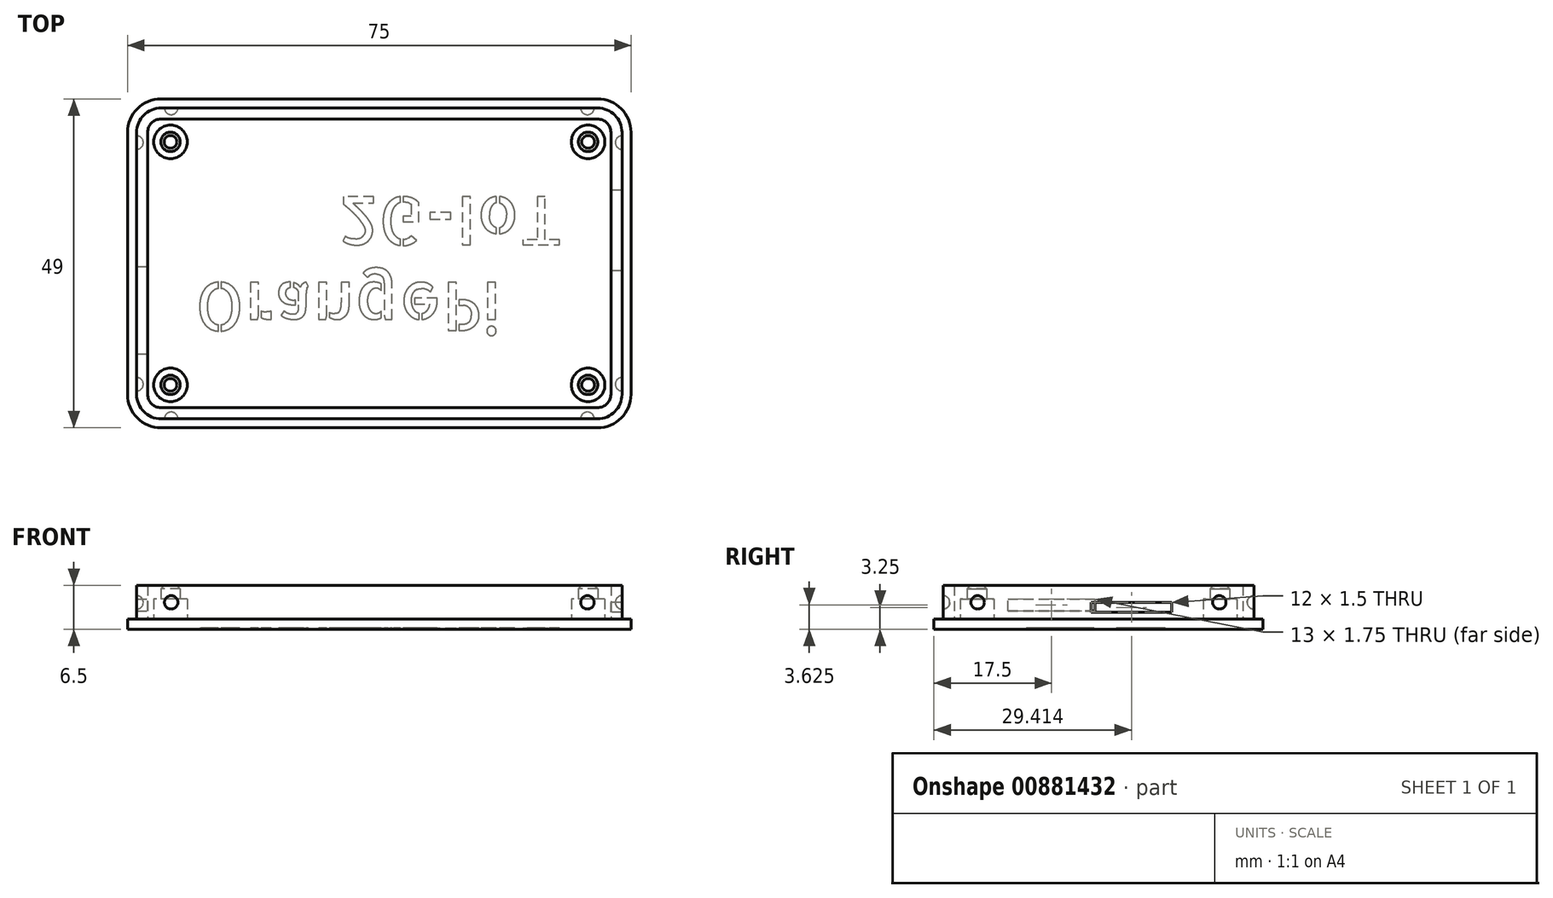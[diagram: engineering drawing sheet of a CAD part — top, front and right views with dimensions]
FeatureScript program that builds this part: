
annotation { "Feature Type Name" : "Feature", "Feature Type Description" : "" }
export const myFeature = defineFeature(function(context is Context, id is Id, definition is map)
    precondition{}
    {
        {
            assignVariable(context, id + "F0", {"name" : "PCBThickness", "anyValue" : 2});
        }
        {
            assignVariable(context, id + "F1", {"name" : "PCBClarence", "anyValue" : 3});
        }
        {
            assignVariable(context, id + "F2", {"name" : "WallThickness", "anyValue" : 3});
        }
        {
            assignVariable(context, id + "F3", {"name" : "OuterFilletRadius", "anyValue" : 5});
        }
        {
            var Q0;
            Q0=qCreatedBy(makeId("Top.planeOp"),FACE);
            var sketch = newSketch(context, id + "F4", { "sketchPlane" : qUnion([Q0])});
            skLineSegment(sketch, "E0.bottom", {"start": v(37.5, 24.5) * mm, "end": v(-37.5, 24.5) * mm});
            skLineSegment(sketch, "E0.top", {"start": v(37.5, -24.5) * mm, "end": v(-37.5, -24.5) * mm});
            skLineSegment(sketch, "E0.left", {"start": v(37.5, 24.5) * mm, "end": v(37.5, -24.5) * mm});
            skLineSegment(sketch, "E0.right", {"start": v(-37.5, 24.5) * mm, "end": v(-37.5, -24.5) * mm});
            skPoint(sketch, "E0.middle", {"position": v(0, 0) * mm});
            skSolve(sketch);
        }
        {
            var Q0;
            Q0 = qSketchRegion(id + "F4", true);
            extrude(context, id + "F5", {"entities" : qUnion([Q0]), "depth" : (getVariable(context, 'WallThickness') + getVariable(context, 'PCBThickness') + getVariable(context, 'PCBClarence')) * mm, "offsetDistance" : 25 * mm});
        }
        {
            var Q0;
            Q0=makeQuery(id+"F5.opExtrude","SWEPT_EDGE",EDGE,{"disambiguationData":[OSD([sQuery(id+"F4.wireOp",EDGE,"E0.top"),sQuery(id+"F4.wireOp",EDGE,"E0.right")])]});
            var Q1;
            Q1=makeQuery(id+"F5.opExtrude","SWEPT_EDGE",EDGE,{"disambiguationData":[OSD([sQuery(id+"F4.wireOp",EDGE,"E0.top"),sQuery(id+"F4.wireOp",EDGE,"E0.left")])]});
            var Q2;
            Q2=makeQuery(id+"F5.opExtrude","SWEPT_EDGE",EDGE,{"disambiguationData":[OSD([sQuery(id+"F4.wireOp",EDGE,"E0.bottom"),sQuery(id+"F4.wireOp",EDGE,"E0.left")])]});
            var Q3;
            Q3=makeQuery(id+"F5.opExtrude","SWEPT_EDGE",EDGE,{"disambiguationData":[OSD([sQuery(id+"F4.wireOp",EDGE,"E0.bottom"),sQuery(id+"F4.wireOp",EDGE,"E0.right")])]});
            fillet(context, id + "F6", {"entities" : qUnion([Q0, Q1, Q2, Q3]), "radius" : (getVariable(context, 'OuterFilletRadius')) * mm, "tangentPropagation" : true, "allowEdgeOverflow" : false});
        }
        {
            var Q0;
            Q0=makeQuery(id+"F5.opExtrude","CAP_FACE",FACE,{"disambiguationData":[OSD([sQuery(id+"F4.wireOp",EDGE,"E0.bottom"),sQuery(id+"F4.wireOp",EDGE,"E0.top"),sQuery(id+"F4.wireOp",EDGE,"E0.left"),sQuery(id+"F4.wireOp",EDGE,"E0.right")])],"isStart":false});
            shell(context, id + "F7", {"entities" : qUnion([Q0]), "thickness" : (getVariable(context, 'WallThickness')) * mm});
        }
        {
            var Q0;
            Q0=makeQuery(id+"F7.opShell","OFFSET_FACE",FACE,{"disambiguationData":[OSD([sQuery(id+"F4.wireOp",EDGE,"E0.bottom"),sQuery(id+"F4.wireOp",EDGE,"E0.top"),sQuery(id+"F4.wireOp",EDGE,"E0.left"),sQuery(id+"F4.wireOp",EDGE,"E0.right")])]});
            var sketch = newSketch(context, id + "F8", { "sketchPlane" : qUnion([Q0])});
            skLineSegment(sketch, "E1.bottom", {"start": v(31.1, 18.1) * mm, "end": v(-31.1, 18.1) * mm, "construction": true});
            skLineSegment(sketch, "E1.top", {"start": v(31.1, -18.1) * mm, "end": v(-31.1, -18.1) * mm, "construction": true});
            skLineSegment(sketch, "E1.left", {"start": v(31.1, 18.1) * mm, "end": v(31.1, -18.1) * mm, "construction": true});
            skLineSegment(sketch, "E1.right", {"start": v(-31.1, 18.1) * mm, "end": v(-31.1, -18.1) * mm, "construction": true});
            skPoint(sketch, "E1.middle", {"position": v(0, 0) * mm});
            skCircle(sketch, "E2", {"center": v(-31.1, 18.1) * mm, "radius": 2.5 * mm});
            skCircle(sketch, "E3", {"center": v(-31.1, -18.1) * mm, "radius": 2.5 * mm});
            skCircle(sketch, "E4", {"center": v(31.1, 18.1) * mm, "radius": 2.5 * mm});
            skCircle(sketch, "E5", {"center": v(31.1, -18.1) * mm, "radius": 2.5 * mm});
            skSolve(sketch);
        }
        {
            var Q0;
            Q0 = qSketchRegion(id + "F8", true);
            extrude(context, id + "F9", {"entities" : qUnion([Q0]), "operationType" : NewBodyOperationType.ADD, "depth" : 3 * mm, "offsetDistance" : 25 * mm});
        }
        {
            var Q0;
            Q0=makeQuery(id+"F9.opExtrude","CAP_FACE",FACE,{"disambiguationData":[OSD([sQuery(id+"F8.wireOp",EDGE,"E2")])],"isStart":false});
            var sketch = newSketch(context, id + "F10", { "sketchPlane" : qUnion([Q0])});
            skLineSegment(sketch, "E6.bottom", {"start": v(-31.1, 18.1) * mm, "end": v(31.1, 18.1) * mm, "construction": true});
            skLineSegment(sketch, "E6.top", {"start": v(-31.1, -18.1) * mm, "end": v(31.1, -18.1) * mm, "construction": true});
            skLineSegment(sketch, "E6.left", {"start": v(-31.1, 18.1) * mm, "end": v(-31.1, -18.1) * mm, "construction": true});
            skLineSegment(sketch, "E6.right", {"start": v(31.1, 18.1) * mm, "end": v(31.1, -18.1) * mm, "construction": true});
            skCircle(sketch, "E7", {"center": v(-31.1, 18.1) * mm, "radius": 1.45 * mm});
            skCircle(sketch, "E8", {"center": v(31.1, 18.1) * mm, "radius": 1.45 * mm});
            skCircle(sketch, "E9", {"center": v(-31.1, -18.1) * mm, "radius": 1.45 * mm});
            skCircle(sketch, "E10", {"center": v(31.1, -18.1) * mm, "radius": 1.45 * mm});
            skSolve(sketch);
        }
        {
            var Q0;
            Q0 = qSketchRegion(id + "F10", true);
            extrude(context, id + "F11", {"entities" : qUnion([Q0]), "operationType" : NewBodyOperationType.ADD, "depth" : 2 * mm, "offsetDistance" : 25 * mm});
        }
        {
            var Q0;
            Q0=makeQuery(id+"F5.opExtrude","CAP_FACE",FACE,{"disambiguationData":[OSD([sQuery(id+"F4.wireOp",EDGE,"E0.bottom"),sQuery(id+"F4.wireOp",EDGE,"E0.top"),sQuery(id+"F4.wireOp",EDGE,"E0.left"),sQuery(id+"F4.wireOp",EDGE,"E0.right")])],"isStart":false});
            var sketch = newSketch(context, id + "F12", { "sketchPlane" : qUnion([Q0])});
            skLineSegment(sketch, "E11", {"start": v(-32.5, 24.5) * mm, "end": v(32.5, 24.5) * mm});
            skLineSegment(sketch, "E12", {"start": v(37.5, 19.5) * mm, "end": v(37.5, -19.5) * mm});
            skLineSegment(sketch, "E13", {"start": v(32.5, -24.5) * mm, "end": v(-32.5, -24.5) * mm});
            skLineSegment(sketch, "E14", {"start": v(-37.5, -19.5) * mm, "end": v(-37.5, 19.5) * mm});
            skArc(sketch, "E15", {"start": v(-32.5, 24.5) * mm, "mid": v(-36.04, 23.04) * mm, "end": v(-37.5, 19.5) * mm});
            skArc(sketch, "E16", {"start": v(37.5, 19.5) * mm, "mid": v(36.04, 23.04) * mm, "end": v(32.5, 24.5) * mm});
            skArc(sketch, "E17", {"start": v(32.5, -24.5) * mm, "mid": v(36.04, -23.04) * mm, "end": v(37.5, -19.5) * mm});
            skArc(sketch, "E18", {"start": v(-37.5, -19.5) * mm, "mid": v(-36.04, -23.04) * mm, "end": v(-32.5, -24.5) * mm});
            skLineSegment(sketch, "E19", {"start": v(-32.5, 24.5) * mm, "end": v(-32.5, 23.15) * mm, "construction": true});
            skLineSegment(sketch, "E20", {"start": v(-32.5, 23.15) * mm, "end": v(32.5, 23.15) * mm});
            skLineSegment(sketch, "E21", {"start": v(32.5, 23.15) * mm, "end": v(32.5, 24.5) * mm, "construction": true});
            skLineSegment(sketch, "E22", {"start": v(37.5, 19.5) * mm, "end": v(36.15, 19.5) * mm, "construction": true});
            skLineSegment(sketch, "E23", {"start": v(36.15, 19.5) * mm, "end": v(36.15, -19.5) * mm});
            skLineSegment(sketch, "E24", {"start": v(36.15, -19.5) * mm, "end": v(37.5, -19.5) * mm, "construction": true});
            skLineSegment(sketch, "E25", {"start": v(32.5, -24.5) * mm, "end": v(32.5, -23.15) * mm, "construction": true});
            skLineSegment(sketch, "E26", {"start": v(32.5, -23.15) * mm, "end": v(-32.5, -23.15) * mm});
            skLineSegment(sketch, "E27", {"start": v(-32.5, -23.15) * mm, "end": v(-32.5, -24.5) * mm, "construction": true});
            skLineSegment(sketch, "E28", {"start": v(-37.5, -19.5) * mm, "end": v(-36.15, -19.5) * mm, "construction": true});
            skLineSegment(sketch, "E29", {"start": v(-36.15, -19.5) * mm, "end": v(-36.15, 19.5) * mm});
            skLineSegment(sketch, "E30", {"start": v(-36.15, 19.5) * mm, "end": v(-37.5, 19.5) * mm, "construction": true});
            skArc(sketch, "E31", {"start": v(-32.5, 23.15) * mm, "mid": v(-35.08, 22.08) * mm, "end": v(-36.15, 19.5) * mm});
            skArc(sketch, "E32", {"start": v(36.15, 19.5) * mm, "mid": v(35.08, 22.08) * mm, "end": v(32.5, 23.15) * mm});
            skArc(sketch, "E33", {"start": v(32.5, -23.15) * mm, "mid": v(35.08, -22.08) * mm, "end": v(36.15, -19.5) * mm});
            skArc(sketch, "E34", {"start": v(-36.15, -19.5) * mm, "mid": v(-35.08, -22.08) * mm, "end": v(-32.5, -23.15) * mm});
            skSolve(sketch);
        }
        {
            var Q0;
            Q0 = qSketchRegion(id + "F12", true);
            extrude(context, id + "F13", {"entities" : qUnion([Q0]), "operationType" : NewBodyOperationType.REMOVE, "oppositeDirection" : true, "depth" : 5 * mm, "offsetDistance" : 25 * mm});
        }
        {
            var Q0;
            Q0=makeQuery(id+"F13.boolean.opBoolean","COPY",FACE,{"derivedFrom":makeQuery(id+"F13.opExtrude","SWEPT_FACE",FACE,{"disambiguationData":[OSD([sQuery(id+"F12.wireOp",EDGE,"E26")])]})});
            var sketch = newSketch(context, id + "F14", { "sketchPlane" : qUnion([Q0])});
            skLineSegment(sketch, "E35", {"start": v(-32.5, 5.5) * mm, "end": v(32.5, 5.5) * mm, "construction": true});
            skCircle(sketch, "E36", {"center": v(-31, 5.5) * mm, "radius": 1 * mm});
            skCircle(sketch, "E37", {"center": v(31, 5.5) * mm, "radius": 1 * mm});
            skSolve(sketch);
        }
        {
            var Q0;
            Q0 = qSketchRegion(id + "F14", true);
            extrude(context, id + "F15", {"entities" : qUnion([Q0]), "operationType" : NewBodyOperationType.REMOVE, "oppositeDirection" : true, "depth" : 1 * mm, "offsetDistance" : 25 * mm});
        }
        {
            var Q0;
            Q0=makeQuery(id+"F13.boolean.opBoolean","COPY",FACE,{"derivedFrom":makeQuery(id+"F13.opExtrude","SWEPT_FACE",FACE,{"disambiguationData":[OSD([sQuery(id+"F12.wireOp",EDGE,"E23")])]})});
            var sketch = newSketch(context, id + "F16", { "sketchPlane" : qUnion([Q0])});
            skLineSegment(sketch, "E38", {"start": v(-19.5, 5.5) * mm, "end": v(19.5, 5.5) * mm, "construction": true});
            skCircle(sketch, "E39", {"center": v(-18, 5.5) * mm, "radius": 1 * mm});
            skCircle(sketch, "E40", {"center": v(18, 5.5) * mm, "radius": 1 * mm});
            skSolve(sketch);
        }
        {
            var Q0;
            Q0 = qSketchRegion(id + "F16", true);
            extrude(context, id + "F17", {"entities" : qUnion([Q0]), "operationType" : NewBodyOperationType.REMOVE, "oppositeDirection" : true, "depth" : 1 * mm, "offsetDistance" : 25 * mm});
        }
        {
            var Q0;
            Q0=makeQuery(id+"F13.boolean.opBoolean","COPY",FACE,{"derivedFrom":makeQuery(id+"F13.opExtrude","SWEPT_FACE",FACE,{"disambiguationData":[OSD([sQuery(id+"F12.wireOp",EDGE,"E20")])]})});
            var sketch = newSketch(context, id + "F18", { "sketchPlane" : qUnion([Q0])});
            skLineSegment(sketch, "E41", {"start": v(-32.5, 5.5) * mm, "end": v(32.5, 5.5) * mm, "construction": true});
            skCircle(sketch, "E42", {"center": v(-31, 5.5) * mm, "radius": 1 * mm});
            skCircle(sketch, "E43", {"center": v(31, 5.5) * mm, "radius": 1 * mm});
            skSolve(sketch);
        }
        {
            var Q0;
            Q0 = qSketchRegion(id + "F18", true);
            extrude(context, id + "F19", {"entities" : qUnion([Q0]), "operationType" : NewBodyOperationType.REMOVE, "oppositeDirection" : true, "depth" : 1 * mm, "offsetDistance" : 25 * mm});
        }
        {
            var Q0;
            Q0=makeQuery(id+"F13.boolean.opBoolean","COPY",FACE,{"derivedFrom":makeQuery(id+"F13.opExtrude","SWEPT_FACE",FACE,{"disambiguationData":[OSD([sQuery(id+"F12.wireOp",EDGE,"E29")])]})});
            var sketch = newSketch(context, id + "F20", { "sketchPlane" : qUnion([Q0])});
            skLineSegment(sketch, "E44", {"start": v(-19.5, 5.5) * mm, "end": v(19.5, 5.5) * mm, "construction": true});
            skCircle(sketch, "E45", {"center": v(-18, 5.5) * mm, "radius": 1 * mm});
            skCircle(sketch, "E46", {"center": v(18, 5.5) * mm, "radius": 1 * mm});
            skSolve(sketch);
        }
        {
            var Q0;
            Q0 = qSketchRegion(id + "F20", true);
            extrude(context, id + "F21", {"entities" : qUnion([Q0]), "operationType" : NewBodyOperationType.REMOVE, "oppositeDirection" : true, "depth" : 1 * mm, "offsetDistance" : 25 * mm});
        }
        {
            var Q0;
            Q0=makeQuery(id+"F21.boolean.opBoolean","COPY",EDGE,{"derivedFrom":makeQuery(id+"F21.opExtrude","CAP_EDGE",EDGE,{"disambiguationData":[OSD([sQuery(id+"F20.wireOp",EDGE,"E45")])],"isStart":false})});
            var Q1;
            Q1=makeQuery(id+"F21.boolean.opBoolean","COPY",EDGE,{"derivedFrom":makeQuery(id+"F21.opExtrude","CAP_EDGE",EDGE,{"disambiguationData":[OSD([sQuery(id+"F20.wireOp",EDGE,"E46")])],"isStart":false})});
            var Q2;
            Q2=makeQuery(id+"F15.boolean.opBoolean","COPY",EDGE,{"derivedFrom":makeQuery(id+"F15.opExtrude","CAP_EDGE",EDGE,{"disambiguationData":[OSD([sQuery(id+"F14.wireOp",EDGE,"E36")])],"isStart":false})});
            var Q3;
            Q3=makeQuery(id+"F15.boolean.opBoolean","COPY",EDGE,{"derivedFrom":makeQuery(id+"F15.opExtrude","CAP_EDGE",EDGE,{"disambiguationData":[OSD([sQuery(id+"F14.wireOp",EDGE,"E37")])],"isStart":false})});
            var Q4;
            Q4=makeQuery(id+"F17.boolean.opBoolean","COPY",EDGE,{"derivedFrom":makeQuery(id+"F17.opExtrude","CAP_EDGE",EDGE,{"disambiguationData":[OSD([sQuery(id+"F16.wireOp",EDGE,"E39")])],"isStart":false})});
            var Q5;
            Q5=makeQuery(id+"F17.boolean.opBoolean","COPY",EDGE,{"derivedFrom":makeQuery(id+"F17.opExtrude","CAP_EDGE",EDGE,{"disambiguationData":[OSD([sQuery(id+"F16.wireOp",EDGE,"E40")])],"isStart":false})});
            var Q6;
            Q6=makeQuery(id+"F19.boolean.opBoolean","COPY",EDGE,{"derivedFrom":makeQuery(id+"F19.opExtrude","CAP_EDGE",EDGE,{"disambiguationData":[OSD([sQuery(id+"F18.wireOp",EDGE,"E42")])],"isStart":false})});
            var Q7;
            Q7=makeQuery(id+"F19.boolean.opBoolean","COPY",EDGE,{"derivedFrom":makeQuery(id+"F19.opExtrude","CAP_EDGE",EDGE,{"disambiguationData":[OSD([sQuery(id+"F18.wireOp",EDGE,"E43")])],"isStart":false})});
            fillet(context, id + "F22", {"entities" : qUnion([Q0, Q1, Q2, Q3, Q4, Q5, Q6, Q7]), "radius" : 1 * mm, "tangentPropagation" : true, "allowEdgeOverflow" : false});
        }
        {
            var Q0;
            Q0=makeQuery(id+"F7.opShell","OFFSET_FACE",FACE,{"disambiguationData":[OSD([sQuery(id+"F4.wireOp",EDGE,"E0.left")])]});
            var sketch = newSketch(context, id + "F23", { "sketchPlane" : qUnion([Q0])});
            skLineSegment(sketch, "E47.bottom", {"start": v(-10.91, 4) * mm, "end": v(1.09, 4) * mm});
            skLineSegment(sketch, "E47.top", {"start": v(-10.91, 5.5) * mm, "end": v(1.09, 5.5) * mm});
            skLineSegment(sketch, "E47.left", {"start": v(-10.91, 4) * mm, "end": v(-10.91, 5.5) * mm});
            skLineSegment(sketch, "E47.right", {"start": v(1.09, 4) * mm, "end": v(1.09, 5.5) * mm});
            skSolve(sketch);
        }
        {
            var Q0;
            Q0 = qSketchRegion(id + "F23", true);
            extrude(context, id + "F24", {"entities" : qUnion([Q0]), "operationType" : NewBodyOperationType.REMOVE, "endBound" : BoundingType.UP_TO_NEXT, "oppositeDirection" : true, "depth" : 25 * mm, "offsetDistance" : 25 * mm});
        }
        {
            var Q0;
            Q0=makeQuery(id+"F7.opShell","OFFSET_FACE",FACE,{"disambiguationData":[OSD([sQuery(id+"F4.wireOp",EDGE,"E0.right")])]});
            var sketch = newSketch(context, id + "F25", { "sketchPlane" : qUnion([Q0])});
            skLineSegment(sketch, "E48.bottom", {"start": v(-13.5, 4.25) * mm, "end": v(-0.5, 4.25) * mm});
            skLineSegment(sketch, "E48.top", {"start": v(-13.5, 6) * mm, "end": v(-0.5, 6) * mm});
            skLineSegment(sketch, "E48.left", {"start": v(-13.5, 4.25) * mm, "end": v(-13.5, 6) * mm});
            skLineSegment(sketch, "E48.right", {"start": v(-0.5, 4.25) * mm, "end": v(-0.5, 6) * mm});
            skSolve(sketch);
        }
        {
            var Q0;
            Q0 = qSketchRegion(id + "F25", true);
            extrude(context, id + "F26", {"entities" : qUnion([Q0]), "operationType" : NewBodyOperationType.REMOVE, "endBound" : BoundingType.UP_TO_NEXT, "oppositeDirection" : true, "depth" : 25 * mm, "offsetDistance" : 25 * mm});
        }
        {
            var Q0;
            Q0=makeQuery(id+"F11.opExtrude","CAP_EDGE",EDGE,{"disambiguationData":[OSD([sQuery(id+"F10.wireOp",EDGE,"E7")])],"isStart":false});
            var Q1;
            Q1=makeQuery(id+"F11.opExtrude","CAP_EDGE",EDGE,{"disambiguationData":[OSD([sQuery(id+"F10.wireOp",EDGE,"E8")])],"isStart":false});
            var Q2;
            Q2=makeQuery(id+"F11.opExtrude","CAP_EDGE",EDGE,{"disambiguationData":[OSD([sQuery(id+"F10.wireOp",EDGE,"E9")])],"isStart":false});
            var Q3;
            Q3=makeQuery(id+"F11.opExtrude","CAP_EDGE",EDGE,{"disambiguationData":[OSD([sQuery(id+"F10.wireOp",EDGE,"E10")])],"isStart":false});
            chamfer(context, id + "F27", {"entities" : qUnion([Q0, Q1, Q2, Q3]), "width" : 0.5 * mm, "tangentPropagation" : true});
        }
        {
            var Q0;
            Q0=makeQuery(id+"F5.opExtrude","CAP_FACE",FACE,{"disambiguationData":[OSD([sQuery(id+"F4.wireOp",EDGE,"E0.bottom"),sQuery(id+"F4.wireOp",EDGE,"E0.top"),sQuery(id+"F4.wireOp",EDGE,"E0.left"),sQuery(id+"F4.wireOp",EDGE,"E0.right")])],"isStart":true});
            var sketch = newSketch(context, id + "F28", { "sketchPlane" : qUnion([Q0])});
            skLineSegment(sketch, "E49", {"start": v(-32.5, 24.5) * mm, "end": v(-37.5, 24.5) * mm, "construction": true});
            skLineSegment(sketch, "E50", {"start": v(-37.5, 24.5) * mm, "end": v(-37.5, 19.5) * mm, "construction": true});
            skLineSegment(sketch, "E51", {"start": v(37.5, -19.5) * mm, "end": v(37.5, -24.5) * mm, "construction": true});
            skLineSegment(sketch, "E52", {"start": v(37.5, -24.5) * mm, "end": v(32.5, -24.5) * mm, "construction": true});
            skLineSegment(sketch, "E53.bottom", {"start": v(-37.5, 24.5) * mm, "end": v(37.5, 24.5) * mm});
            skLineSegment(sketch, "E53.top", {"start": v(-37.5, -24.5) * mm, "end": v(37.5, -24.5) * mm});
            skLineSegment(sketch, "E53.left", {"start": v(-37.5, 24.5) * mm, "end": v(-37.5, -24.5) * mm});
            skLineSegment(sketch, "E53.right", {"start": v(37.5, 24.5) * mm, "end": v(37.5, -24.5) * mm});
            skSolve(sketch);
        }
        {
            var Q0;
            Q0 = qSketchRegion(id + "F28", true);
            extrude(context, id + "F29", {"entities" : qUnion([Q0]), "operationType" : NewBodyOperationType.REMOVE, "oppositeDirection" : true, "depth" : 1.5 * mm, "offsetDistance" : 25 * mm});
        }
        {
            var Q0;
            Q0=makeQuery(id+"F29.boolean.opBoolean","COPY",FACE,{"derivedFrom":makeQuery(id+"F29.opExtrude","CAP_FACE",FACE,{"disambiguationData":[OSD([sQuery(id+"F28.wireOp",EDGE,"E53.bottom"),sQuery(id+"F28.wireOp",EDGE,"E53.top"),sQuery(id+"F28.wireOp",EDGE,"E53.left"),sQuery(id+"F28.wireOp",EDGE,"E53.right")])],"isStart":false})});
            var sketch = newSketch(context, id + "F30", { "sketchPlane" : qUnion([Q0])});
            skLineSegment(sketch, "E54", {"start": v(-37.5, 19.5) * mm, "end": v(-27.5, 10) * mm, "construction": true});
            skLineSegment(sketch, "E55", {"start": v(37.5, 19.5) * mm, "end": v(27.5, 10) * mm, "construction": true});
            skText(sketch, "E56", { "text": "OrangePi\n        2G-IoT", "fontName": "AllertaStencil-Regular.ttf"});
            skLineSegment(sketch, "E57", {"start": v(-27.5, 2.83) * mm, "end": v(-27.5, -10) * mm, "construction": true});
            skLineSegment(sketch, "E58", {"start": v(-27.5, -10) * mm, "end": v(27.5, -10) * mm, "construction": true});
            skLineSegment(sketch, "E59", {"start": v(27.5, -10) * mm, "end": v(27.5, 2.83) * mm, "construction": true});
            skLineSegment(sketch, "E60", {"start": v(-37.5, -19.5) * mm, "end": v(-27.5, -10) * mm, "construction": true});
            skLineSegment(sketch, "E61", {"start": v(37.5, -19.5) * mm, "end": v(27.5, -10) * mm, "construction": true});
            const initialGuessF30  = {"E56": [-0.0275, 0.00283, 1, 0, 0.00717]};
            skSetInitialGuess(sketch, initialGuessF30);
            skSolve(sketch);
        }
        {
            var Q0;
            Q0 = qSketchRegion(id + "F30", true);
            extrude(context, id + "F31", {"entities" : qUnion([Q0]), "operationType" : NewBodyOperationType.REMOVE, "oppositeDirection" : true, "depth" : 0.16 * mm, "offsetDistance" : 25 * mm});
        }
    });
